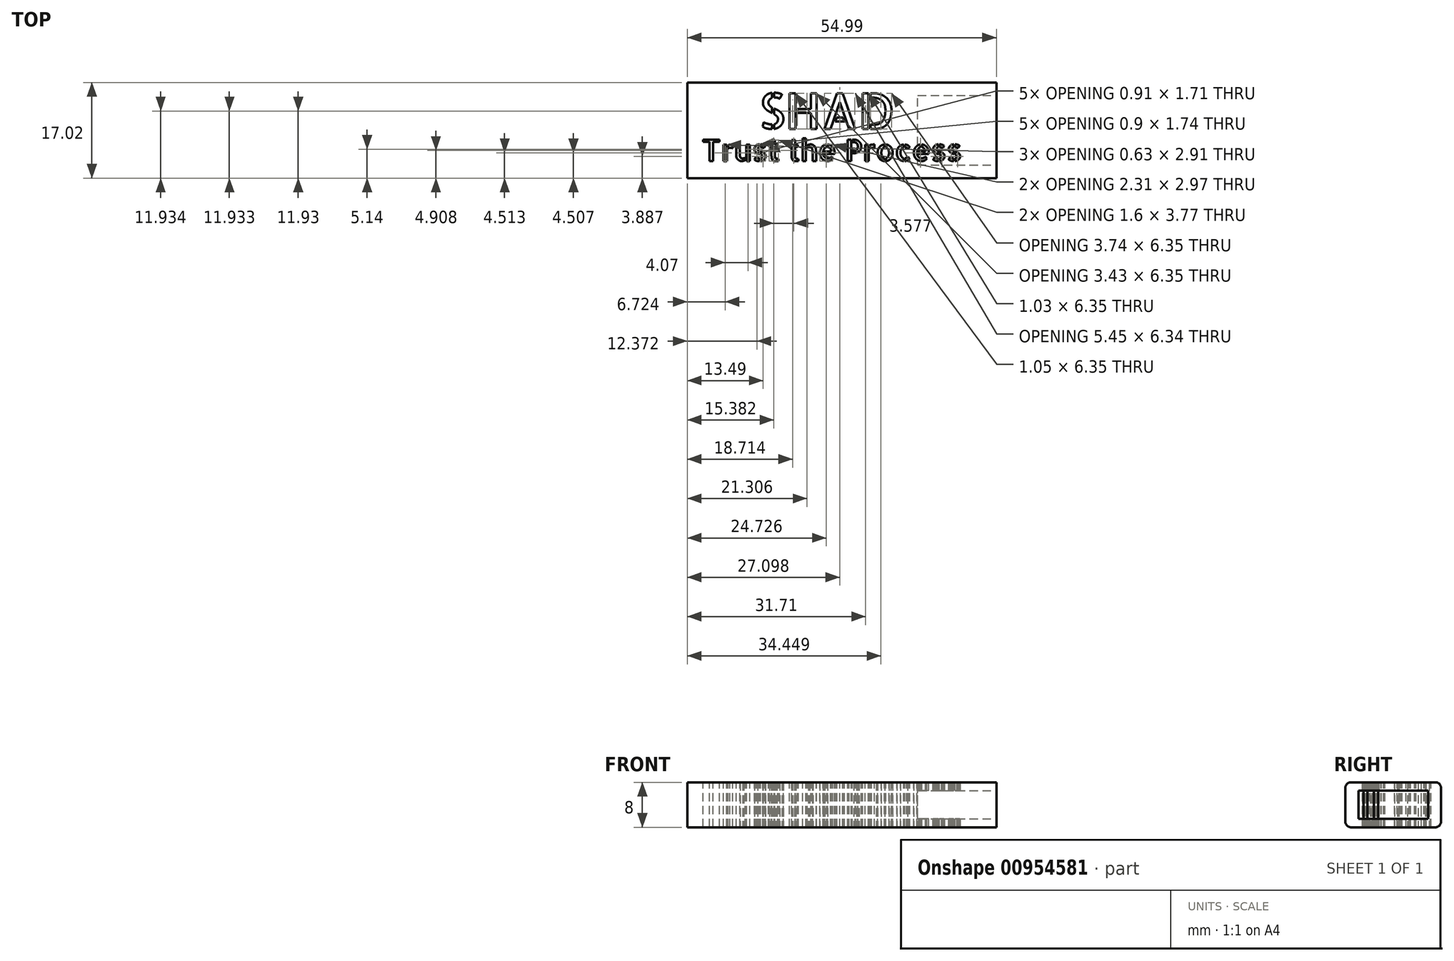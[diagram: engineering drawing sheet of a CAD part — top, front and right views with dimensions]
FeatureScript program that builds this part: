
annotation { "Feature Type Name" : "Feature", "Feature Type Description" : "" }
export const myFeature = defineFeature(function(context is Context, id is Id, definition is map)
    precondition{}
    {
        {
            var Q0;
            Q0=qCreatedBy(makeId("Front.planeOp"),FACE);
            var sketch = newSketch(context, id + "F0", { "sketchPlane" : qUnion([Q0])});
            skLineSegment(sketch, "E0.bottom", {"start": v(-7.52, -4) * mm, "end": v(7.52, -4) * mm});
            skLineSegment(sketch, "E0.top", {"start": v(-7.52, 4) * mm, "end": v(7.52, 4) * mm});
            skLineSegment(sketch, "E0.left", {"start": v(-8.5, -3) * mm, "end": v(-8.5, 3) * mm});
            skLineSegment(sketch, "E0.right", {"start": v(8.5, -3) * mm, "end": v(8.5, 3) * mm});
            skPoint(sketch, "E1.visualSharp", {"position": v(-8.5, 4) * mm});
            skArc(sketch, "E1.filletArc", {"start": v(-7.52, 4) * mm, "mid": v(-8.22, 3.71) * mm, "end": v(-8.5, 3) * mm});
            skPoint(sketch, "E2.visualSharp", {"position": v(8.5, 4) * mm});
            skArc(sketch, "E2.filletArc", {"start": v(8.5, 3) * mm, "mid": v(8.22, 3.71) * mm, "end": v(7.52, 4) * mm});
            skPoint(sketch, "E3.visualSharp", {"position": v(8.5, -4) * mm});
            skArc(sketch, "E3.filletArc", {"start": v(7.52, -4) * mm, "mid": v(8.22, -3.71) * mm, "end": v(8.5, -3) * mm});
            skPoint(sketch, "E4.visualSharp", {"position": v(-8.5, -4) * mm});
            skArc(sketch, "E4.filletArc", {"start": v(-8.5, -3) * mm, "mid": v(-8.22, -3.71) * mm, "end": v(-7.52, -4) * mm});
            skSolve(sketch);
        }
        {
            var Q0;
            Q0=qSketchRegion(id+"F0",true);
            extrude(context, id + "F1", {"entities" : qUnion([Q0]), "depth" : 55 * mm, "offsetDistance" : 25.4 * mm});
        }
        {
            var Q0;
            Q0=makeQuery(id+"F1.opExtrude","CAP_FACE",FACE,{"disambiguationData":[OSD([sQuery(id+"F0.wireOp",EDGE,"E0.bottom"),sQuery(id+"F0.wireOp",EDGE,"E0.top"),sQuery(id+"F0.wireOp",EDGE,"E0.left"),sQuery(id+"F0.wireOp",EDGE,"E0.right"),sQuery(id+"F0.wireOp",EDGE,"E1.filletArc"),sQuery(id+"F0.wireOp",EDGE,"E2.filletArc"),sQuery(id+"F0.wireOp",EDGE,"E3.filletArc"),sQuery(id+"F0.wireOp",EDGE,"E4.filletArc")])],"isStart":false});
            var sketch = newSketch(context, id + "F2", { "sketchPlane" : qUnion([Q0])});
            skLineSegment(sketch, "E5.bottom", {"start": v(-6.2, 2.5) * mm, "end": v(6.2, 2.5) * mm});
            skLineSegment(sketch, "E5.top", {"start": v(-6.2, -2.5) * mm, "end": v(6.2, -2.5) * mm});
            skLineSegment(sketch, "E5.left", {"start": v(-6.2, 2.5) * mm, "end": v(-6.2, -2.5) * mm});
            skLineSegment(sketch, "E5.right", {"start": v(6.2, 2.5) * mm, "end": v(6.2, -2.5) * mm});
            skSolve(sketch);
        }
        {
            var Q0;
            Q0=qSketchRegion(id+"F2",true);
            extrude(context, id + "F3", {"entities" : qUnion([Q0]), "operationType" : NewBodyOperationType.REMOVE, "oppositeDirection" : true, "depth" : 14 * mm, "offsetDistance" : 25.4 * mm});
        }
        {
            var Q0;
            Q0=makeQuery(id+"F1.opExtrude","SWEPT_BODY",BODY,{"disambiguationData":[OSD([sQuery(id+"F0.wireOp",EDGE,"E0.bottom"),sQuery(id+"F0.wireOp",EDGE,"E0.top"),sQuery(id+"F0.wireOp",EDGE,"E0.left"),sQuery(id+"F0.wireOp",EDGE,"E0.right"),sQuery(id+"F0.wireOp",EDGE,"E1.filletArc"),sQuery(id+"F0.wireOp",EDGE,"E2.filletArc"),sQuery(id+"F0.wireOp",EDGE,"E3.filletArc"),sQuery(id+"F0.wireOp",EDGE,"E4.filletArc")])]});
            var Q1;
            Q1=makeQuery(id+"F1.opExtrude","CAP_EDGE",EDGE,{"disambiguationData":[OSD([sQuery(id+"F0.wireOp",EDGE,"E0.left")])],"isStart":true});
            transform(context, id + "F4", {"entities" : qUnion([Q0]), "transformType" : TransformType.ROTATION, "transformAxis" : qUnion([Q1]), "angle" : 90 * degree, "makeCopy" : false});
        }
        {
            var Q0;
            Q0=makeQuery(id+"F1.opExtrude","SWEPT_FACE",FACE,{"disambiguationData":[OSD([sQuery(id+"F0.wireOp",EDGE,"E0.top")])]});
            var sketch = newSketch(context, id + "F5", { "sketchPlane" : qUnion([Q0])});
            skText(sketch, "E6", { "text": "SHAD", "fontName": "AllertaStencil-Regular.ttf"});
            skText(sketch, "E7", { "text": "Trust the Process\n", "fontName": "AllertaStencil-Regular.ttf"});
            const initialGuessF5  = {"E6": [0.0042, 0.00876, 1, 0, 0.00635], "E7": [-0.00597, 0.00305, 1, 0, 0.00381]};
            skSetInitialGuess(sketch, initialGuessF5);
            skSolve(sketch);
        }
        {
            var Q0;
            Q0=qSketchRegion(id+"F5",true);
            extrude(context, id + "F6", {"entities" : qUnion([Q0]), "operationType" : NewBodyOperationType.REMOVE, "oppositeDirection" : true, "depth" : 11.43 * mm, "offsetDistance" : 25.4 * mm});
        }
    });
